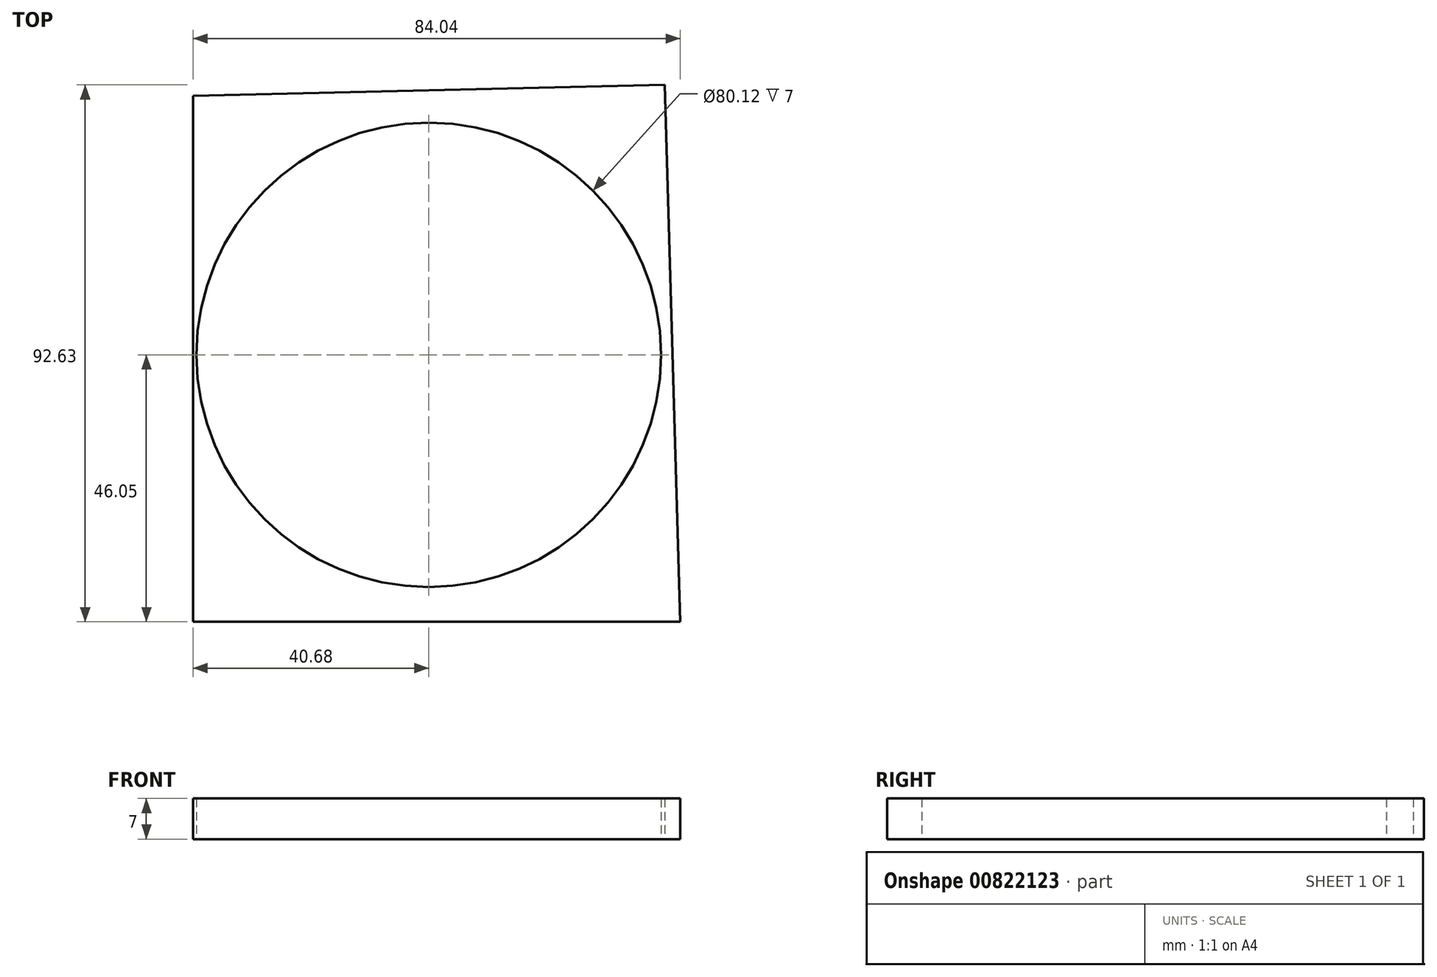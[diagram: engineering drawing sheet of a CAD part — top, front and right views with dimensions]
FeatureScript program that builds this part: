
annotation { "Feature Type Name" : "Feature", "Feature Type Description" : "" }
export const myFeature = defineFeature(function(context is Context, id is Id, definition is map)
    precondition{}
    {
        {
            var Q0;
            Q0=qCreatedBy(makeId("Top.planeOp"),FACE);
            var sketch = newSketch(context, id + "F0", { "sketchPlane" : qUnion([Q0])});
            skCircle(sketch, "E0", {"center": v(0, 0) * mm, "radius": 12.43 * mm});
            skCircle(sketch, "E1", {"center": v(0, 0) * mm, "radius": 40.06 * mm});
            skCircle(sketch, "E2", {"center": v(0, 0) * mm, "radius": 5.52 * mm});
            skCircle(sketch, "E3", {"center": v(0, 0) * mm, "radius": 17.47 * mm});
            skCircle(sketch, "E4", {"center": v(0, 0) * mm, "radius": 22.3 * mm});
            skCircle(sketch, "E5", {"center": v(0, 0) * mm, "radius": 25.88 * mm});
            skCircle(sketch, "E6", {"center": v(0, 0) * mm, "radius": 29.55 * mm});
            skCircle(sketch, "E7", {"center": v(0, 0) * mm, "radius": 33.68 * mm});
            skCircle(sketch, "E8", {"center": v(0, 0) * mm, "radius": 36.14 * mm});
            skLineSegment(sketch, "E9", {"start": v(-40.68, 44.7) * mm, "end": v(-40.68, -46.05) * mm});
            skLineSegment(sketch, "E10", {"start": v(-40.68, -46.05) * mm, "end": v(43.36, -46.05) * mm});
            skLineSegment(sketch, "E11", {"start": v(43.36, -46.05) * mm, "end": v(40.68, 46.58) * mm});
            skLineSegment(sketch, "E12", {"start": v(40.68, 46.58) * mm, "end": v(-40.68, 44.7) * mm});
            skSolve(sketch);
        }
        {
            var Q0;
            Q0 = qSketchRegion(id + "F0", true);
            extrude(context, id + "F1", {"entities" : qUnion([Q0]), "depth" : 7 * mm, "offsetDistance" : 25.4 * mm});
        }
    });
